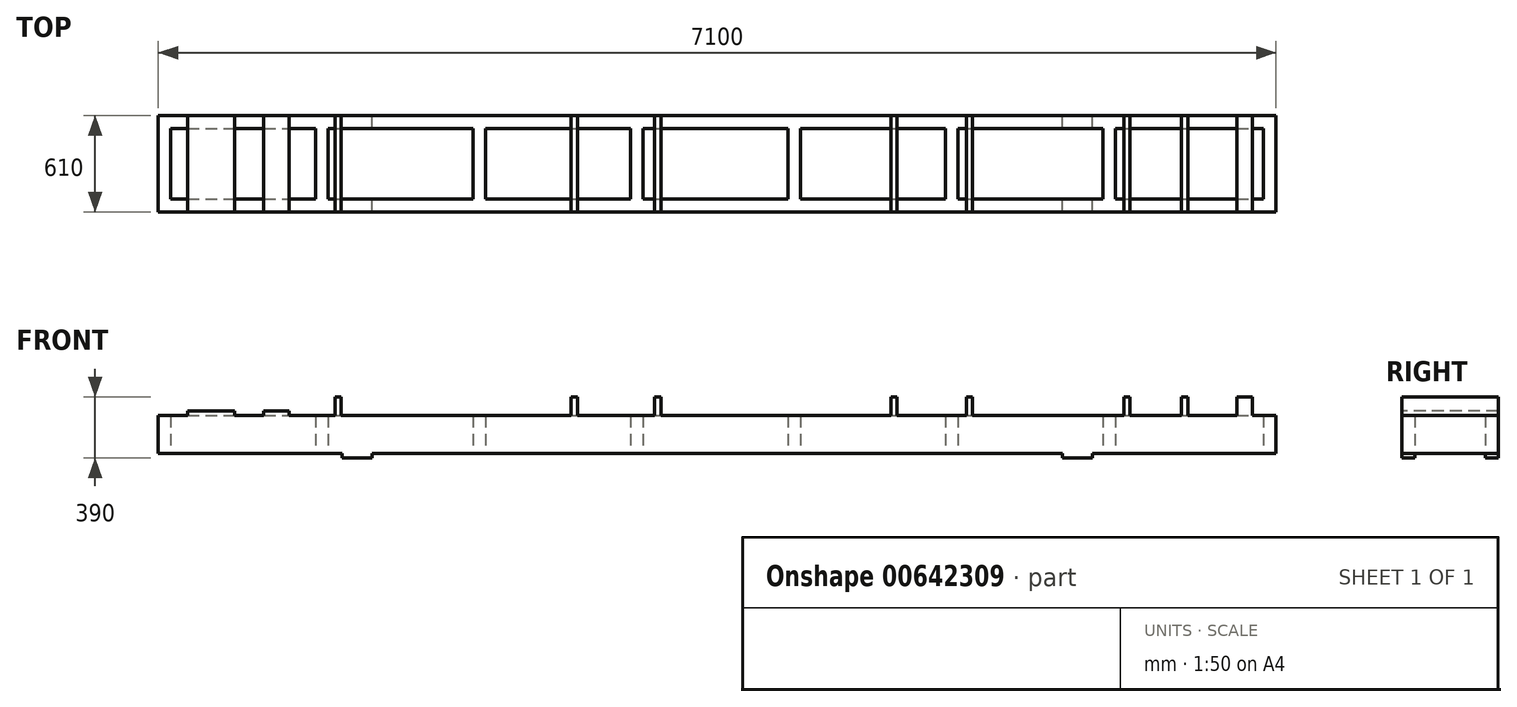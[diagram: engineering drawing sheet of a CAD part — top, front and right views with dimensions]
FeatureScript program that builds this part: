
annotation { "Feature Type Name" : "Feature", "Feature Type Description" : "" }
export const myFeature = defineFeature(function(context is Context, id is Id, definition is map)
    precondition{}
    {
        {
            var Q0;
            Q0=qCreatedBy(makeId("Top.planeOp"),FACE);
            var sketch = newSketch(context, id + "F0", { "sketchPlane" : qUnion([Q0])});
            skLineSegment(sketch, "E0.bottom", {"start": v(0, 0) * mm, "end": v(7100, 0) * mm});
            skLineSegment(sketch, "E0.top", {"start": v(0, 610) * mm, "end": v(7100, 610) * mm});
            skLineSegment(sketch, "E0.left", {"start": v(0, 0) * mm, "end": v(0, 610) * mm});
            skLineSegment(sketch, "E0.right", {"start": v(7100, 0) * mm, "end": v(7100, 610) * mm});
            skLineSegment(sketch, "E1.bottom", {"start": v(80, 530) * mm, "end": v(1000, 530) * mm});
            skLineSegment(sketch, "E1.top", {"start": v(80, 80) * mm, "end": v(1000, 80) * mm});
            skLineSegment(sketch, "E1.left", {"start": v(80, 530) * mm, "end": v(80, 80) * mm});
            skLineSegment(sketch, "E1.right", {"start": v(1000, 530) * mm, "end": v(1000, 80) * mm});
            skLineSegment(sketch, "E2.bottom", {"start": v(1080, 530) * mm, "end": v(2000, 530) * mm});
            skLineSegment(sketch, "E2.top", {"start": v(1080, 80) * mm, "end": v(2000, 80) * mm});
            skLineSegment(sketch, "E2.left", {"start": v(1080, 530) * mm, "end": v(1080, 80) * mm});
            skLineSegment(sketch, "E2.right", {"start": v(2000, 530) * mm, "end": v(2000, 80) * mm});
            skLineSegment(sketch, "E3.bottom", {"start": v(2080, 530) * mm, "end": v(3000, 530) * mm});
            skLineSegment(sketch, "E3.top", {"start": v(2080, 80) * mm, "end": v(3000, 80) * mm});
            skLineSegment(sketch, "E3.left", {"start": v(2080, 530) * mm, "end": v(2080, 80) * mm});
            skLineSegment(sketch, "E3.right", {"start": v(3000, 530) * mm, "end": v(3000, 80) * mm});
            skLineSegment(sketch, "E4.bottom", {"start": v(3080, 530) * mm, "end": v(4000, 530) * mm});
            skLineSegment(sketch, "E4.top", {"start": v(3080, 80) * mm, "end": v(4000, 80) * mm});
            skLineSegment(sketch, "E4.left", {"start": v(3080, 530) * mm, "end": v(3080, 80) * mm});
            skLineSegment(sketch, "E4.right", {"start": v(4000, 530) * mm, "end": v(4000, 80) * mm});
            skLineSegment(sketch, "E5.bottom", {"start": v(4080, 530) * mm, "end": v(5000, 530) * mm});
            skLineSegment(sketch, "E5.top", {"start": v(4080, 80) * mm, "end": v(5000, 80) * mm});
            skLineSegment(sketch, "E5.left", {"start": v(4080, 530) * mm, "end": v(4080, 80) * mm});
            skLineSegment(sketch, "E5.right", {"start": v(5000, 530) * mm, "end": v(5000, 80) * mm});
            skLineSegment(sketch, "E6.bottom", {"start": v(5080, 530) * mm, "end": v(6000, 530) * mm});
            skLineSegment(sketch, "E6.top", {"start": v(5080, 80) * mm, "end": v(6000, 80) * mm});
            skLineSegment(sketch, "E6.left", {"start": v(5080, 530) * mm, "end": v(5080, 80) * mm});
            skLineSegment(sketch, "E6.right", {"start": v(6000, 530) * mm, "end": v(6000, 80) * mm});
            skLineSegment(sketch, "E7.bottom", {"start": v(6080, 530) * mm, "end": v(7020, 530) * mm});
            skLineSegment(sketch, "E7.top", {"start": v(6080, 80) * mm, "end": v(7020, 80) * mm});
            skLineSegment(sketch, "E7.left", {"start": v(6080, 530) * mm, "end": v(6080, 80) * mm});
            skLineSegment(sketch, "E7.right", {"start": v(7020, 530) * mm, "end": v(7020, 80) * mm});
            skLineSegment(sketch, "E8", {"start": v(1000, 530) * mm, "end": v(1080, 530) * mm, "construction": true});
            skLineSegment(sketch, "E9", {"start": v(2000, 530) * mm, "end": v(2080, 530) * mm, "construction": true});
            skLineSegment(sketch, "E10", {"start": v(3000, 530) * mm, "end": v(3080, 530) * mm, "construction": true});
            skLineSegment(sketch, "E11", {"start": v(4000, 530) * mm, "end": v(4080, 530) * mm, "construction": true});
            skLineSegment(sketch, "E12", {"start": v(5000, 530) * mm, "end": v(5080, 530) * mm, "construction": true});
            skLineSegment(sketch, "E13", {"start": v(6000, 530) * mm, "end": v(6080, 530) * mm, "construction": true});
            skLineSegment(sketch, "E14", {"start": v(4080, 530) * mm, "end": v(4080, 610) * mm, "construction": true});
            skLineSegment(sketch, "E15", {"start": v(4080, 610) * mm, "end": v(4080, 80) * mm, "construction": true});
            skLineSegment(sketch, "E16", {"start": v(4080, 0) * mm, "end": v(4080, 80) * mm, "construction": true});
            skSolve(sketch);
        }
        {
            var Q0;
            Q0=makeQuery(id+"F0.imprint","IMPRINT",FACE,{"disambiguationData":[TD([[makeQuery(id+"F0.imprint","IMPRINT",EDGE,{"derivedFrom":sQuery(id+"F0.wireOp",EDGE,"E0.bottom")}),1.0]])]});
            extrude(context, id + "F1", {"entities" : qUnion([Q0]), "depth" : 240 * mm, "offsetDistance" : 25 * mm});
        }
        {
            var Q0;
            Q0=makeQuery(id+"F1.opExtrude","CAP_FACE",FACE,{"disambiguationData":[OSD([sQuery(id+"F0.wireOp",EDGE,"E0.bottom"),sQuery(id+"F0.wireOp",EDGE,"E0.top"),sQuery(id+"F0.wireOp",EDGE,"E0.left"),sQuery(id+"F0.wireOp",EDGE,"E0.right"),sQuery(id+"F0.wireOp",EDGE,"E1.bottom"),sQuery(id+"F0.wireOp",EDGE,"E1.top"),sQuery(id+"F0.wireOp",EDGE,"E1.left"),sQuery(id+"F0.wireOp",EDGE,"E1.right"),sQuery(id+"F0.wireOp",EDGE,"E2.bottom"),sQuery(id+"F0.wireOp",EDGE,"E2.top"),sQuery(id+"F0.wireOp",EDGE,"E2.left"),sQuery(id+"F0.wireOp",EDGE,"E2.right"),sQuery(id+"F0.wireOp",EDGE,"E3.bottom"),sQuery(id+"F0.wireOp",EDGE,"E3.top"),sQuery(id+"F0.wireOp",EDGE,"E3.left"),sQuery(id+"F0.wireOp",EDGE,"E3.right"),sQuery(id+"F0.wireOp",EDGE,"E4.bottom"),sQuery(id+"F0.wireOp",EDGE,"E4.top"),sQuery(id+"F0.wireOp",EDGE,"E4.left"),sQuery(id+"F0.wireOp",EDGE,"E4.right"),sQuery(id+"F0.wireOp",EDGE,"E5.bottom"),sQuery(id+"F0.wireOp",EDGE,"E5.top"),sQuery(id+"F0.wireOp",EDGE,"E5.left"),sQuery(id+"F0.wireOp",EDGE,"E5.right"),sQuery(id+"F0.wireOp",EDGE,"E6.bottom"),sQuery(id+"F0.wireOp",EDGE,"E6.top"),sQuery(id+"F0.wireOp",EDGE,"E6.left"),sQuery(id+"F0.wireOp",EDGE,"E6.right"),sQuery(id+"F0.wireOp",EDGE,"E7.bottom"),sQuery(id+"F0.wireOp",EDGE,"E7.top"),sQuery(id+"F0.wireOp",EDGE,"E7.left"),sQuery(id+"F0.wireOp",EDGE,"E7.right")])],"isStart":true});
            var sketch = newSketch(context, id + "F2", { "sketchPlane" : qUnion([Q0])});
            skLineSegment(sketch, "E17.bottom", {"start": v(1167.5, 0) * mm, "end": v(1358.14, 0) * mm});
            skLineSegment(sketch, "E17.top", {"start": v(1167.5, -80) * mm, "end": v(1358.14, -80) * mm});
            skLineSegment(sketch, "E17.left", {"start": v(1167.5, 0) * mm, "end": v(1167.5, -80) * mm});
            skLineSegment(sketch, "E17.right", {"start": v(1358.14, 0) * mm, "end": v(1358.14, -80) * mm});
            skLineSegment(sketch, "E18.bottom", {"start": v(1167.5, -530) * mm, "end": v(1358.14, -530) * mm});
            skLineSegment(sketch, "E18.top", {"start": v(1167.5, -610) * mm, "end": v(1358.14, -610) * mm});
            skLineSegment(sketch, "E18.left", {"start": v(1167.5, -530) * mm, "end": v(1167.5, -610) * mm});
            skLineSegment(sketch, "E18.right", {"start": v(1358.14, -530) * mm, "end": v(1358.14, -610) * mm});
            skLineSegment(sketch, "E19.bottom", {"start": v(5741.86, 0) * mm, "end": v(5932.5, 0) * mm});
            skLineSegment(sketch, "E19.top", {"start": v(5741.86, -80) * mm, "end": v(5932.5, -80) * mm});
            skLineSegment(sketch, "E19.left", {"start": v(5741.86, 0) * mm, "end": v(5741.86, -80) * mm});
            skLineSegment(sketch, "E19.right", {"start": v(5932.5, 0) * mm, "end": v(5932.5, -80) * mm});
            skLineSegment(sketch, "E20.bottom", {"start": v(5741.86, -530) * mm, "end": v(5932.5, -530) * mm});
            skLineSegment(sketch, "E20.top", {"start": v(5741.86, -610) * mm, "end": v(5932.5, -610) * mm});
            skLineSegment(sketch, "E20.left", {"start": v(5741.86, -530) * mm, "end": v(5741.86, -610) * mm});
            skLineSegment(sketch, "E20.right", {"start": v(5932.5, -530) * mm, "end": v(5932.5, -610) * mm});
            skSolve(sketch);
        }
        {
            var Q0;
            Q0=makeQuery(id+"F2.imprint","IMPRINT",FACE,{"disambiguationData":[TD([[makeQuery(id+"F2.imprint","IMPRINT",EDGE,{"derivedFrom":sQuery(id+"F2.wireOp",EDGE,"E17.bottom")}),-1.0]])]});
            var Q1;
            Q1=makeQuery(id+"F2.imprint","IMPRINT",FACE,{"disambiguationData":[TD([[makeQuery(id+"F2.imprint","IMPRINT",EDGE,{"derivedFrom":sQuery(id+"F2.wireOp",EDGE,"E18.bottom")}),-1.0]])]});
            var Q2;
            Q2=makeQuery(id+"F2.imprint","IMPRINT",FACE,{"disambiguationData":[TD([[makeQuery(id+"F2.imprint","IMPRINT",EDGE,{"derivedFrom":sQuery(id+"F2.wireOp",EDGE,"E20.bottom")}),-1.0]])]});
            var Q3;
            Q3=makeQuery(id+"F2.imprint","IMPRINT",FACE,{"disambiguationData":[TD([[makeQuery(id+"F2.imprint","IMPRINT",EDGE,{"derivedFrom":sQuery(id+"F2.wireOp",EDGE,"E19.bottom")}),-1.0]])]});
            extrude(context, id + "F3", {"entities" : qUnion([Q0, Q1, Q2, Q3]), "operationType" : NewBodyOperationType.ADD, "depth" : 30 * mm, "offsetDistance" : 25 * mm});
        }
        {
            var Q0;
            Q0=makeQuery(id+"F1.opExtrude","CAP_FACE",FACE,{"disambiguationData":[OSD([sQuery(id+"F0.wireOp",EDGE,"E0.bottom"),sQuery(id+"F0.wireOp",EDGE,"E0.top"),sQuery(id+"F0.wireOp",EDGE,"E0.left"),sQuery(id+"F0.wireOp",EDGE,"E0.right"),sQuery(id+"F0.wireOp",EDGE,"E1.bottom"),sQuery(id+"F0.wireOp",EDGE,"E1.top"),sQuery(id+"F0.wireOp",EDGE,"E1.left"),sQuery(id+"F0.wireOp",EDGE,"E1.right"),sQuery(id+"F0.wireOp",EDGE,"E2.bottom"),sQuery(id+"F0.wireOp",EDGE,"E2.top"),sQuery(id+"F0.wireOp",EDGE,"E2.left"),sQuery(id+"F0.wireOp",EDGE,"E2.right"),sQuery(id+"F0.wireOp",EDGE,"E3.bottom"),sQuery(id+"F0.wireOp",EDGE,"E3.top"),sQuery(id+"F0.wireOp",EDGE,"E3.left"),sQuery(id+"F0.wireOp",EDGE,"E3.right"),sQuery(id+"F0.wireOp",EDGE,"E4.bottom"),sQuery(id+"F0.wireOp",EDGE,"E4.top"),sQuery(id+"F0.wireOp",EDGE,"E4.left"),sQuery(id+"F0.wireOp",EDGE,"E4.right"),sQuery(id+"F0.wireOp",EDGE,"E5.bottom"),sQuery(id+"F0.wireOp",EDGE,"E5.top"),sQuery(id+"F0.wireOp",EDGE,"E5.left"),sQuery(id+"F0.wireOp",EDGE,"E5.right"),sQuery(id+"F0.wireOp",EDGE,"E6.bottom"),sQuery(id+"F0.wireOp",EDGE,"E6.top"),sQuery(id+"F0.wireOp",EDGE,"E6.left"),sQuery(id+"F0.wireOp",EDGE,"E6.right"),sQuery(id+"F0.wireOp",EDGE,"E7.bottom"),sQuery(id+"F0.wireOp",EDGE,"E7.top"),sQuery(id+"F0.wireOp",EDGE,"E7.left"),sQuery(id+"F0.wireOp",EDGE,"E7.right")])],"isStart":false});
            var sketch = newSketch(context, id + "F4", { "sketchPlane" : qUnion([Q0])});
            skLineSegment(sketch, "E21.bottom", {"start": v(185.5, 610) * mm, "end": v(485.5, 610) * mm});
            skLineSegment(sketch, "E21.top", {"start": v(185.5, 0) * mm, "end": v(485.5, 0) * mm});
            skLineSegment(sketch, "E21.left", {"start": v(185.5, 610) * mm, "end": v(185.5, 0) * mm});
            skLineSegment(sketch, "E21.right", {"start": v(485.5, 610) * mm, "end": v(485.5, 0) * mm});
            skLineSegment(sketch, "E22.bottom", {"start": v(670.5, 610) * mm, "end": v(830.5, 610) * mm});
            skLineSegment(sketch, "E22.top", {"start": v(670.5, 0) * mm, "end": v(830.5, 0) * mm});
            skLineSegment(sketch, "E22.left", {"start": v(670.5, 610) * mm, "end": v(670.5, 0) * mm});
            skLineSegment(sketch, "E22.right", {"start": v(830.5, 610) * mm, "end": v(830.5, 0) * mm});
            skLineSegment(sketch, "E23.bottom", {"start": v(1122.5, 610) * mm, "end": v(1162.5, 610) * mm});
            skLineSegment(sketch, "E23.top", {"start": v(1122.5, 0) * mm, "end": v(1162.5, 0) * mm});
            skLineSegment(sketch, "E23.left", {"start": v(1122.5, 610) * mm, "end": v(1122.5, 0) * mm});
            skLineSegment(sketch, "E23.right", {"start": v(1162.5, 610) * mm, "end": v(1162.5, 0) * mm});
            skLineSegment(sketch, "E24.bottom", {"start": v(2622.5, 610) * mm, "end": v(2662.5, 610) * mm});
            skLineSegment(sketch, "E24.top", {"start": v(2622.5, 0) * mm, "end": v(2662.5, 0) * mm});
            skLineSegment(sketch, "E24.left", {"start": v(2622.5, 610) * mm, "end": v(2622.5, 0) * mm});
            skLineSegment(sketch, "E24.right", {"start": v(2662.5, 610) * mm, "end": v(2662.5, 0) * mm});
            skLineSegment(sketch, "E25.bottom", {"start": v(3152.5, 610) * mm, "end": v(3192.5, 610) * mm});
            skLineSegment(sketch, "E25.top", {"start": v(3152.5, 0) * mm, "end": v(3192.5, 0) * mm});
            skLineSegment(sketch, "E25.left", {"start": v(3152.5, 610) * mm, "end": v(3152.5, 0) * mm});
            skLineSegment(sketch, "E25.right", {"start": v(3192.5, 610) * mm, "end": v(3192.5, 0) * mm});
            skLineSegment(sketch, "E26.bottom", {"start": v(4652.5, 610) * mm, "end": v(4692.5, 610) * mm});
            skLineSegment(sketch, "E26.top", {"start": v(4652.5, 0) * mm, "end": v(4692.5, 0) * mm});
            skLineSegment(sketch, "E26.left", {"start": v(4652.5, 610) * mm, "end": v(4652.5, 0) * mm});
            skLineSegment(sketch, "E26.right", {"start": v(4692.5, 610) * mm, "end": v(4692.5, 0) * mm});
            skLineSegment(sketch, "E27.bottom", {"start": v(5132.5, 610) * mm, "end": v(5172.5, 610) * mm});
            skLineSegment(sketch, "E27.top", {"start": v(5132.5, 0) * mm, "end": v(5172.5, 0) * mm});
            skLineSegment(sketch, "E27.left", {"start": v(5132.5, 610) * mm, "end": v(5132.5, 0) * mm});
            skLineSegment(sketch, "E27.right", {"start": v(5172.5, 610) * mm, "end": v(5172.5, 0) * mm});
            skLineSegment(sketch, "E28.bottom", {"start": v(6132.5, 610) * mm, "end": v(6172.5, 610) * mm});
            skLineSegment(sketch, "E28.top", {"start": v(6132.5, 0) * mm, "end": v(6172.5, 0) * mm});
            skLineSegment(sketch, "E28.left", {"start": v(6132.5, 610) * mm, "end": v(6132.5, 0) * mm});
            skLineSegment(sketch, "E28.right", {"start": v(6172.5, 610) * mm, "end": v(6172.5, 0) * mm});
            skLineSegment(sketch, "E29.bottom", {"start": v(6500, 610) * mm, "end": v(6540, 610) * mm});
            skLineSegment(sketch, "E29.top", {"start": v(6500, 0) * mm, "end": v(6540, 0) * mm});
            skLineSegment(sketch, "E29.left", {"start": v(6500, 610) * mm, "end": v(6500, 0) * mm});
            skLineSegment(sketch, "E29.right", {"start": v(6540, 610) * mm, "end": v(6540, 0) * mm});
            skLineSegment(sketch, "E30.bottom", {"start": v(6850, 610) * mm, "end": v(6950, 610) * mm});
            skLineSegment(sketch, "E30.top", {"start": v(6850, 0) * mm, "end": v(6950, 0) * mm});
            skLineSegment(sketch, "E30.left", {"start": v(6850, 610) * mm, "end": v(6850, 0) * mm});
            skLineSegment(sketch, "E30.right", {"start": v(6950, 610) * mm, "end": v(6950, 0) * mm});
            skSolve(sketch);
        }
        {
            var Q0;
            {var subQ0=sQuery(id+"F4.wireOp",EDGE,"E30.bottom");Q0=makeQuery(id+"F4.imprint","IMPRINT",FACE,{"disambiguationData":[TD([[makeQuery(id+"F4.imprint","IMPRINT",EDGE,{"derivedFrom":subQ0}),-1.0]])]});}
            var Q1;
            {var subQ0=sQuery(id+"F4.wireOp",EDGE,"E30.left");var subQ1=makeQuery(id+"F1.opExtrude","CAP_EDGE",EDGE,{"disambiguationData":[OSD([sQuery(id+"F0.wireOp",EDGE,"E7.bottom")])],"isStart":false});var subQ2=makeQuery(id+"F4.imprint","INTERSECT",VERTEX,{"derivedFrom":[subQ1,subQ0]});Q1=makeQuery(id+"F4.imprint","IMPRINT",FACE,{"disambiguationData":[TD([[makeQuery(id+"F4.imprint","IMPRINT",EDGE,{"disambiguationData":[TD([[subQ2,-1.0]])],"derivedFrom":subQ0}),1.0]])]});}
            var Q2;
            {var subQ0=sQuery(id+"F4.wireOp",EDGE,"E30.top");Q2=makeQuery(id+"F4.imprint","IMPRINT",FACE,{"disambiguationData":[TD([[makeQuery(id+"F4.imprint","IMPRINT",EDGE,{"derivedFrom":subQ0}),1.0]])]});}
            var Q3;
            {var subQ0=sQuery(id+"F4.wireOp",EDGE,"E29.top");Q3=makeQuery(id+"F4.imprint","IMPRINT",FACE,{"disambiguationData":[TD([[makeQuery(id+"F4.imprint","IMPRINT",EDGE,{"derivedFrom":subQ0}),1.0]])]});}
            var Q4;
            {var subQ0=sQuery(id+"F4.wireOp",EDGE,"E29.left");var subQ1=makeQuery(id+"F1.opExtrude","CAP_EDGE",EDGE,{"disambiguationData":[OSD([sQuery(id+"F0.wireOp",EDGE,"E7.bottom")])],"isStart":false});var subQ2=makeQuery(id+"F4.imprint","INTERSECT",VERTEX,{"derivedFrom":[subQ1,subQ0]});Q4=makeQuery(id+"F4.imprint","IMPRINT",FACE,{"disambiguationData":[TD([[makeQuery(id+"F4.imprint","IMPRINT",EDGE,{"disambiguationData":[TD([[subQ2,-1.0]])],"derivedFrom":subQ0}),1.0]])]});}
            var Q5;
            {var subQ0=sQuery(id+"F4.wireOp",EDGE,"E29.bottom");Q5=makeQuery(id+"F4.imprint","IMPRINT",FACE,{"disambiguationData":[TD([[makeQuery(id+"F4.imprint","IMPRINT",EDGE,{"derivedFrom":subQ0}),-1.0]])]});}
            var Q6;
            {var subQ0=sQuery(id+"F4.wireOp",EDGE,"E28.bottom");Q6=makeQuery(id+"F4.imprint","IMPRINT",FACE,{"disambiguationData":[TD([[makeQuery(id+"F4.imprint","IMPRINT",EDGE,{"derivedFrom":subQ0}),-1.0]])]});}
            var Q7;
            {var subQ0=sQuery(id+"F4.wireOp",EDGE,"E28.left");var subQ1=makeQuery(id+"F1.opExtrude","CAP_EDGE",EDGE,{"disambiguationData":[OSD([sQuery(id+"F0.wireOp",EDGE,"E7.bottom")])],"isStart":false});var subQ2=makeQuery(id+"F4.imprint","INTERSECT",VERTEX,{"derivedFrom":[subQ1,subQ0]});Q7=makeQuery(id+"F4.imprint","IMPRINT",FACE,{"disambiguationData":[TD([[makeQuery(id+"F4.imprint","IMPRINT",EDGE,{"disambiguationData":[TD([[subQ2,-1.0]])],"derivedFrom":subQ0}),1.0]])]});}
            var Q8;
            {var subQ0=sQuery(id+"F4.wireOp",EDGE,"E28.top");Q8=makeQuery(id+"F4.imprint","IMPRINT",FACE,{"disambiguationData":[TD([[makeQuery(id+"F4.imprint","IMPRINT",EDGE,{"derivedFrom":subQ0}),1.0]])]});}
            var Q9;
            {var subQ0=sQuery(id+"F4.wireOp",EDGE,"E27.top");Q9=makeQuery(id+"F4.imprint","IMPRINT",FACE,{"disambiguationData":[TD([[makeQuery(id+"F4.imprint","IMPRINT",EDGE,{"derivedFrom":subQ0}),1.0]])]});}
            var Q10;
            {var subQ0=sQuery(id+"F4.wireOp",EDGE,"E27.left");var subQ1=makeQuery(id+"F1.opExtrude","CAP_EDGE",EDGE,{"disambiguationData":[OSD([sQuery(id+"F0.wireOp",EDGE,"E6.bottom")])],"isStart":false});var subQ2=makeQuery(id+"F4.imprint","INTERSECT",VERTEX,{"derivedFrom":[subQ1,subQ0]});Q10=makeQuery(id+"F4.imprint","IMPRINT",FACE,{"disambiguationData":[TD([[makeQuery(id+"F4.imprint","IMPRINT",EDGE,{"disambiguationData":[TD([[subQ2,-1.0]])],"derivedFrom":subQ0}),1.0]])]});}
            var Q11;
            {var subQ0=sQuery(id+"F4.wireOp",EDGE,"E27.bottom");Q11=makeQuery(id+"F4.imprint","IMPRINT",FACE,{"disambiguationData":[TD([[makeQuery(id+"F4.imprint","IMPRINT",EDGE,{"derivedFrom":subQ0}),-1.0]])]});}
            var Q12;
            {var subQ0=sQuery(id+"F4.wireOp",EDGE,"E26.bottom");Q12=makeQuery(id+"F4.imprint","IMPRINT",FACE,{"disambiguationData":[TD([[makeQuery(id+"F4.imprint","IMPRINT",EDGE,{"derivedFrom":subQ0}),-1.0]])]});}
            var Q13;
            {var subQ0=sQuery(id+"F4.wireOp",EDGE,"E26.left");var subQ1=makeQuery(id+"F1.opExtrude","CAP_EDGE",EDGE,{"disambiguationData":[OSD([sQuery(id+"F0.wireOp",EDGE,"E5.bottom")])],"isStart":false});var subQ2=makeQuery(id+"F4.imprint","INTERSECT",VERTEX,{"derivedFrom":[subQ1,subQ0]});Q13=makeQuery(id+"F4.imprint","IMPRINT",FACE,{"disambiguationData":[TD([[makeQuery(id+"F4.imprint","IMPRINT",EDGE,{"disambiguationData":[TD([[subQ2,-1.0]])],"derivedFrom":subQ0}),1.0]])]});}
            var Q14;
            {var subQ0=sQuery(id+"F4.wireOp",EDGE,"E26.top");Q14=makeQuery(id+"F4.imprint","IMPRINT",FACE,{"disambiguationData":[TD([[makeQuery(id+"F4.imprint","IMPRINT",EDGE,{"derivedFrom":subQ0}),1.0]])]});}
            var Q15;
            {var subQ0=sQuery(id+"F4.wireOp",EDGE,"E25.top");Q15=makeQuery(id+"F4.imprint","IMPRINT",FACE,{"disambiguationData":[TD([[makeQuery(id+"F4.imprint","IMPRINT",EDGE,{"derivedFrom":subQ0}),1.0]])]});}
            var Q16;
            {var subQ0=sQuery(id+"F4.wireOp",EDGE,"E25.left");var subQ1=makeQuery(id+"F1.opExtrude","CAP_EDGE",EDGE,{"disambiguationData":[OSD([sQuery(id+"F0.wireOp",EDGE,"E4.bottom")])],"isStart":false});var subQ2=makeQuery(id+"F4.imprint","INTERSECT",VERTEX,{"derivedFrom":[subQ1,subQ0]});Q16=makeQuery(id+"F4.imprint","IMPRINT",FACE,{"disambiguationData":[TD([[makeQuery(id+"F4.imprint","IMPRINT",EDGE,{"disambiguationData":[TD([[subQ2,-1.0]])],"derivedFrom":subQ0}),1.0]])]});}
            var Q17;
            {var subQ0=sQuery(id+"F4.wireOp",EDGE,"E25.bottom");Q17=makeQuery(id+"F4.imprint","IMPRINT",FACE,{"disambiguationData":[TD([[makeQuery(id+"F4.imprint","IMPRINT",EDGE,{"derivedFrom":subQ0}),-1.0]])]});}
            var Q18;
            {var subQ0=sQuery(id+"F4.wireOp",EDGE,"E24.top");Q18=makeQuery(id+"F4.imprint","IMPRINT",FACE,{"disambiguationData":[TD([[makeQuery(id+"F4.imprint","IMPRINT",EDGE,{"derivedFrom":subQ0}),1.0]])]});}
            var Q19;
            {var subQ0=sQuery(id+"F4.wireOp",EDGE,"E24.left");var subQ1=makeQuery(id+"F1.opExtrude","CAP_EDGE",EDGE,{"disambiguationData":[OSD([sQuery(id+"F0.wireOp",EDGE,"E3.bottom")])],"isStart":false});var subQ2=makeQuery(id+"F4.imprint","INTERSECT",VERTEX,{"derivedFrom":[subQ1,subQ0]});Q19=makeQuery(id+"F4.imprint","IMPRINT",FACE,{"disambiguationData":[TD([[makeQuery(id+"F4.imprint","IMPRINT",EDGE,{"disambiguationData":[TD([[subQ2,-1.0]])],"derivedFrom":subQ0}),1.0]])]});}
            var Q20;
            {var subQ0=sQuery(id+"F4.wireOp",EDGE,"E24.bottom");Q20=makeQuery(id+"F4.imprint","IMPRINT",FACE,{"disambiguationData":[TD([[makeQuery(id+"F4.imprint","IMPRINT",EDGE,{"derivedFrom":subQ0}),-1.0]])]});}
            var Q21;
            {var subQ0=sQuery(id+"F4.wireOp",EDGE,"E23.top");Q21=makeQuery(id+"F4.imprint","IMPRINT",FACE,{"disambiguationData":[TD([[makeQuery(id+"F4.imprint","IMPRINT",EDGE,{"derivedFrom":subQ0}),1.0]])]});}
            var Q22;
            {var subQ0=sQuery(id+"F4.wireOp",EDGE,"E23.left");var subQ1=makeQuery(id+"F1.opExtrude","CAP_EDGE",EDGE,{"disambiguationData":[OSD([sQuery(id+"F0.wireOp",EDGE,"E2.bottom")])],"isStart":false});var subQ2=makeQuery(id+"F4.imprint","INTERSECT",VERTEX,{"derivedFrom":[subQ1,subQ0]});Q22=makeQuery(id+"F4.imprint","IMPRINT",FACE,{"disambiguationData":[TD([[makeQuery(id+"F4.imprint","IMPRINT",EDGE,{"disambiguationData":[TD([[subQ2,-1.0]])],"derivedFrom":subQ0}),1.0]])]});}
            var Q23;
            {var subQ0=sQuery(id+"F4.wireOp",EDGE,"E23.bottom");Q23=makeQuery(id+"F4.imprint","IMPRINT",FACE,{"disambiguationData":[TD([[makeQuery(id+"F4.imprint","IMPRINT",EDGE,{"derivedFrom":subQ0}),-1.0]])]});}
            extrude(context, id + "F5", {"entities" : qUnion([Q0, Q1, Q2, Q3, Q4, Q5, Q6, Q7, Q8, Q9, Q10, Q11, Q12, Q13, Q14, Q15, Q16, Q17, Q18, Q19, Q20, Q21, Q22, Q23]), "operationType" : NewBodyOperationType.ADD, "depth" : 120 * mm, "offsetDistance" : 25 * mm});
        }
        {
            var Q0;
            {var subQ0=sQuery(id+"F4.wireOp",EDGE,"E21.bottom");Q0=makeQuery(id+"F4.imprint","IMPRINT",FACE,{"disambiguationData":[TD([[makeQuery(id+"F4.imprint","IMPRINT",EDGE,{"derivedFrom":subQ0}),-1.0]])]});}
            var Q1;
            {var subQ0=sQuery(id+"F4.wireOp",EDGE,"E21.left");var subQ1=makeQuery(id+"F1.opExtrude","CAP_EDGE",EDGE,{"disambiguationData":[OSD([sQuery(id+"F0.wireOp",EDGE,"E1.bottom")])],"isStart":false});var subQ2=makeQuery(id+"F4.imprint","INTERSECT",VERTEX,{"derivedFrom":[subQ1,subQ0]});Q1=makeQuery(id+"F4.imprint","IMPRINT",FACE,{"disambiguationData":[TD([[makeQuery(id+"F4.imprint","IMPRINT",EDGE,{"disambiguationData":[TD([[subQ2,-1.0]])],"derivedFrom":subQ0}),1.0]])]});}
            var Q2;
            {var subQ0=sQuery(id+"F4.wireOp",EDGE,"E21.top");Q2=makeQuery(id+"F4.imprint","IMPRINT",FACE,{"disambiguationData":[TD([[makeQuery(id+"F4.imprint","IMPRINT",EDGE,{"derivedFrom":subQ0}),1.0]])]});}
            var Q3;
            {var subQ0=sQuery(id+"F4.wireOp",EDGE,"E22.top");Q3=makeQuery(id+"F4.imprint","IMPRINT",FACE,{"disambiguationData":[TD([[makeQuery(id+"F4.imprint","IMPRINT",EDGE,{"derivedFrom":subQ0}),1.0]])]});}
            var Q4;
            {var subQ0=sQuery(id+"F4.wireOp",EDGE,"E22.left");var subQ1=makeQuery(id+"F1.opExtrude","CAP_EDGE",EDGE,{"disambiguationData":[OSD([sQuery(id+"F0.wireOp",EDGE,"E1.bottom")])],"isStart":false});var subQ2=makeQuery(id+"F4.imprint","INTERSECT",VERTEX,{"derivedFrom":[subQ1,subQ0]});Q4=makeQuery(id+"F4.imprint","IMPRINT",FACE,{"disambiguationData":[TD([[makeQuery(id+"F4.imprint","IMPRINT",EDGE,{"disambiguationData":[TD([[subQ2,-1.0]])],"derivedFrom":subQ0}),1.0]])]});}
            var Q5;
            {var subQ0=sQuery(id+"F4.wireOp",EDGE,"E22.bottom");Q5=makeQuery(id+"F4.imprint","IMPRINT",FACE,{"disambiguationData":[TD([[makeQuery(id+"F4.imprint","IMPRINT",EDGE,{"derivedFrom":subQ0}),-1.0]])]});}
            extrude(context, id + "F6", {"entities" : qUnion([Q0, Q1, Q2, Q3, Q4, Q5]), "operationType" : NewBodyOperationType.ADD, "depth" : 30 * mm, "offsetDistance" : 25 * mm});
        }
    });
